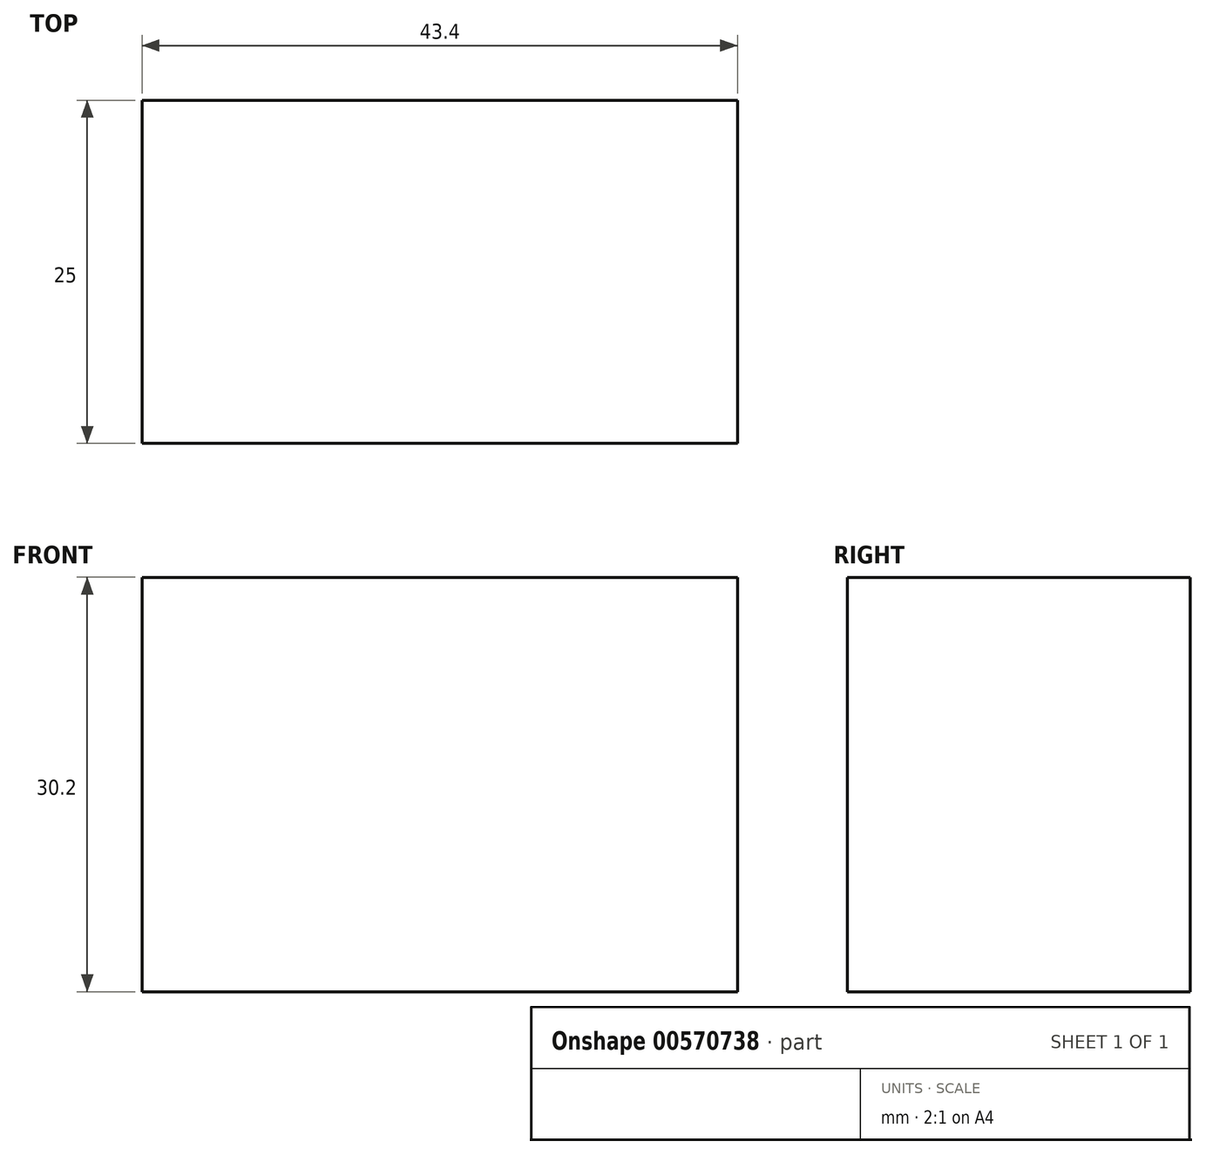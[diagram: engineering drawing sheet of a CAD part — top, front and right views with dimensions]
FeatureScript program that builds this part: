
annotation { "Feature Type Name" : "Feature", "Feature Type Description" : "" }
export const myFeature = defineFeature(function(context is Context, id is Id, definition is map)
    precondition{}
    {
        {
            var Q0;
            Q0=qCreatedBy(makeId("Front.planeOp"),FACE);
            var sketch = newSketch(context, id + "F0", { "sketchPlane" : qUnion([Q0])});
            skLineSegment(sketch, "E0.bottom", {"start": v(-112.49, 36.96) * mm, "end": v(-69.1, 36.96) * mm});
            skLineSegment(sketch, "E0.top", {"start": v(-112.49, 6.76) * mm, "end": v(-69.1, 6.76) * mm});
            skLineSegment(sketch, "E0.left", {"start": v(-112.49, 36.96) * mm, "end": v(-112.49, 6.76) * mm});
            skLineSegment(sketch, "E0.right", {"start": v(-69.1, 36.96) * mm, "end": v(-69.1, 6.76) * mm});
            skSolve(sketch);
        }
        {
            var Q0;
            Q0=qSketchRegion(id+"F0",true);
            extrude(context, id + "F1", {"entities" : qUnion([Q0]), "depth" : 25 * mm, "offsetDistance" : 25 * mm});
        }
    });
